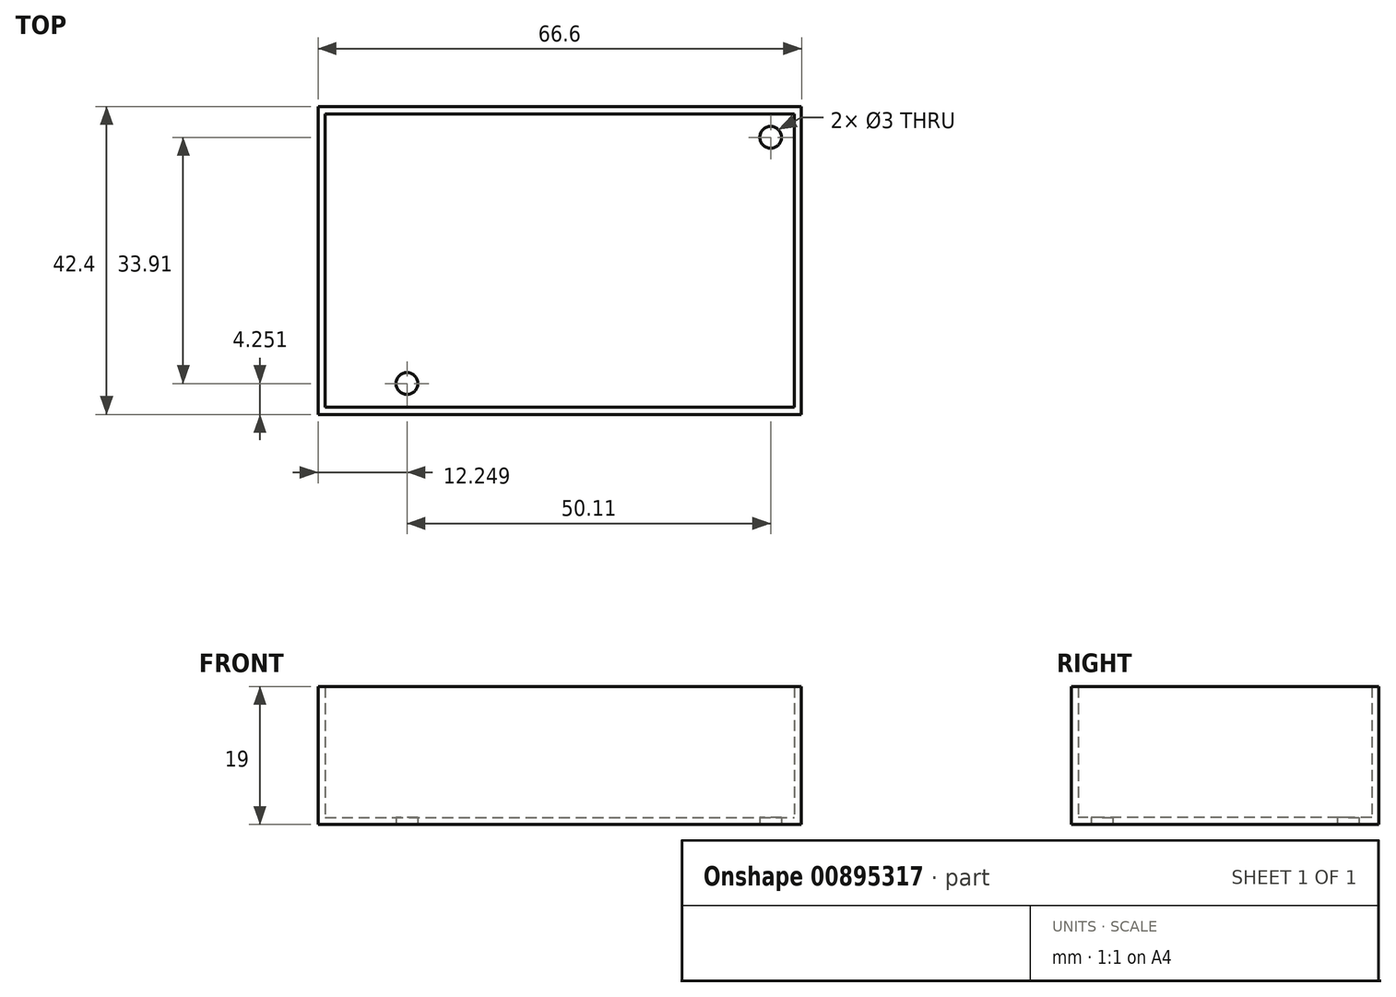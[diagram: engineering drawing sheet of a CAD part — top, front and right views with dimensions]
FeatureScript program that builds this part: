
annotation { "Feature Type Name" : "Feature", "Feature Type Description" : "" }
export const myFeature = defineFeature(function(context is Context, id is Id, definition is map)
    precondition{}
    {
        {
            var Q0;
            Q0=qCreatedBy(makeId("Top.planeOp"),FACE);
            var sketch = newSketch(context, id + "F0", { "sketchPlane" : qUnion([Q0])});
            skLineSegment(sketch, "E0.bottom", {"start": v(-23.6, 12.15) * mm, "end": v(43, 12.15) * mm});
            skLineSegment(sketch, "E0.top", {"start": v(-23.6, -30.25) * mm, "end": v(43, -30.25) * mm});
            skLineSegment(sketch, "E0.left", {"start": v(-23.6, 12.15) * mm, "end": v(-23.6, -30.25) * mm});
            skLineSegment(sketch, "E0.right", {"start": v(43, 12.15) * mm, "end": v(43, -30.25) * mm});
            skSolve(sketch);
        }
        {
            var Q0;
            Q0=makeQuery(id+"F0.imprint","IMPRINT",FACE,{"disambiguationData":[TD([[makeQuery(id+"F0.imprint","IMPRINT",EDGE,{"derivedFrom":sQuery(id+"F0.wireOp",EDGE,"E0.bottom")}),-1.0]])]});
            extrude(context, id + "F1", {"entities" : qUnion([Q0]), "depth" : 19 * mm, "offsetDistance" : 25 * mm});
        }
        {
            var Q0;
            Q0=makeQuery(id+"F1.opExtrude","CAP_FACE",FACE,{"disambiguationData":[OSD([sQuery(id+"F0.wireOp",EDGE,"E0.bottom"),sQuery(id+"F0.wireOp",EDGE,"E0.top"),sQuery(id+"F0.wireOp",EDGE,"E0.left"),sQuery(id+"F0.wireOp",EDGE,"E0.right")])],"isStart":false});
            shell(context, id + "F2", {"entities" : qUnion([Q0]), "thickness" : 1 * mm});
        }
        {
            var Q0;
            Q0=makeQuery(id+"F1.opExtrude","CAP_FACE",FACE,{"disambiguationData":[OSD([sQuery(id+"F0.wireOp",EDGE,"E0.bottom"),sQuery(id+"F0.wireOp",EDGE,"E0.top"),sQuery(id+"F0.wireOp",EDGE,"E0.left"),sQuery(id+"F0.wireOp",EDGE,"E0.right")])],"isStart":true});
            var sketch = newSketch(context, id + "F3", { "sketchPlane" : qUnion([Q0])});
            skPoint(sketch, "E1", {"position": v(-11.35, 26) * mm});
            skCircle(sketch, "E2", {"center": v(-11.35, 26) * mm, "radius": 1.5 * mm});
            skSolve(sketch);
        }
        {
            var Q0;
            Q0 = qSketchRegion(id + "F3", true);
            extrude(context, id + "F4", {"entities" : qUnion([Q0]), "operationType" : NewBodyOperationType.REMOVE, "oppositeDirection" : true, "depth" : 25 * mm, "offsetDistance" : 25 * mm});
        }
        {
            var Q0;
            Q0=makeQuery(id+"F1.opExtrude","CAP_FACE",FACE,{"disambiguationData":[OSD([sQuery(id+"F0.wireOp",EDGE,"E0.bottom"),sQuery(id+"F0.wireOp",EDGE,"E0.top"),sQuery(id+"F0.wireOp",EDGE,"E0.left"),sQuery(id+"F0.wireOp",EDGE,"E0.right")])],"isStart":true});
            var sketch = newSketch(context, id + "F5", { "sketchPlane" : qUnion([Q0])});
            skPoint(sketch, "E3", {"position": v(38.76, -7.91) * mm});
            skCircle(sketch, "E4", {"center": v(38.76, -7.91) * mm, "radius": 1.5 * mm});
            skSolve(sketch);
        }
        {
            var Q0;
            Q0 = qSketchRegion(id + "F5", true);
            extrude(context, id + "F6", {"entities" : qUnion([Q0]), "operationType" : NewBodyOperationType.REMOVE, "oppositeDirection" : true, "depth" : 25 * mm, "offsetDistance" : 25 * mm});
        }
    });
